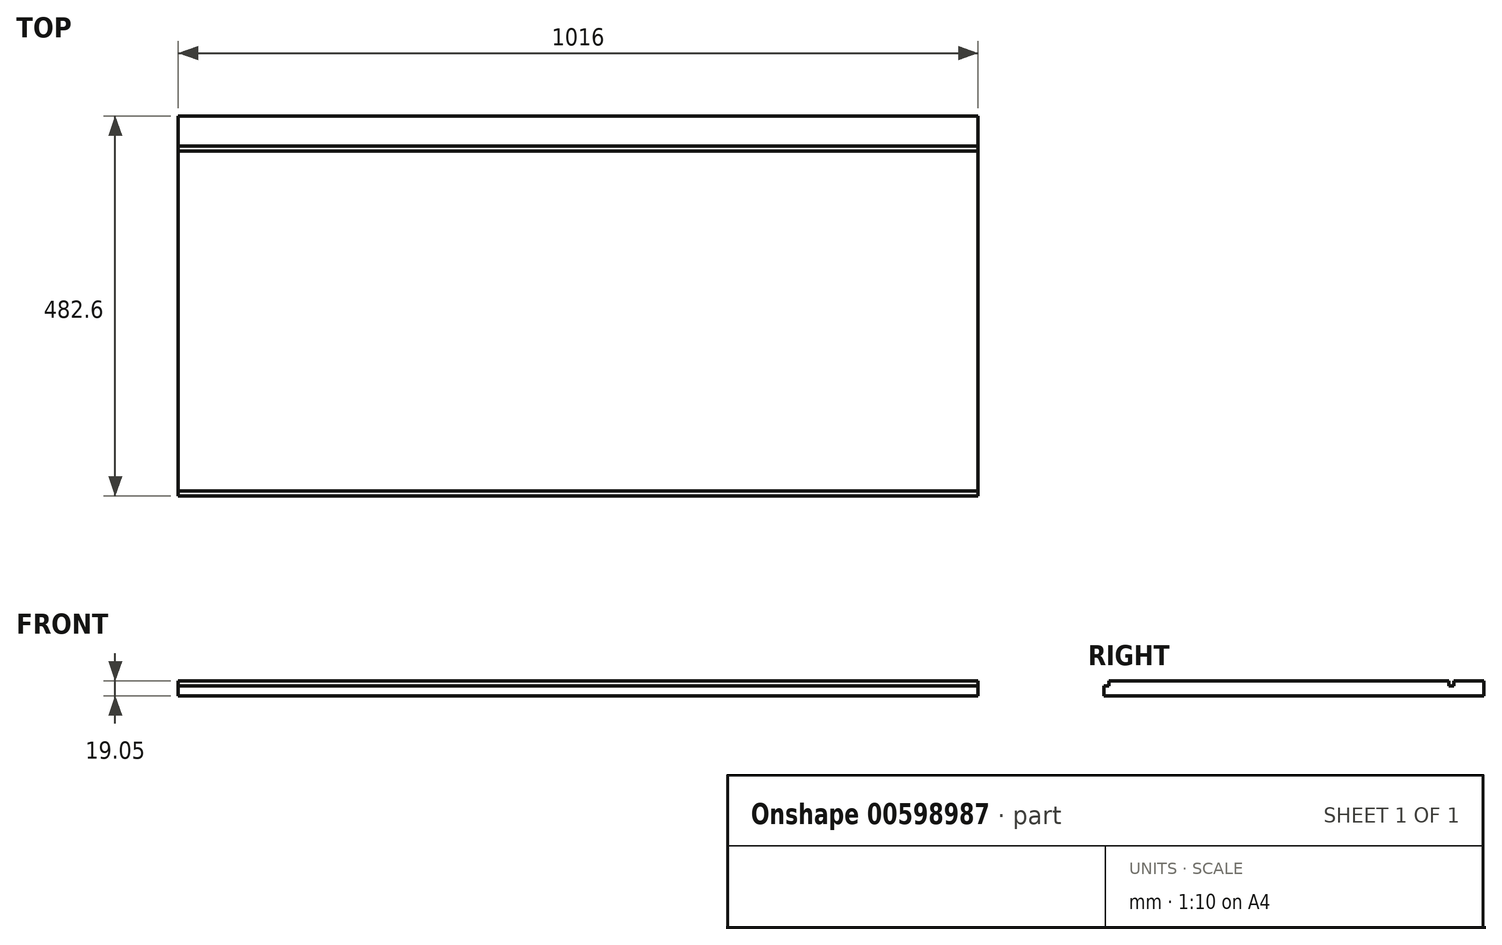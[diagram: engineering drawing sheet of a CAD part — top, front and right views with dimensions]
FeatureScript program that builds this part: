
annotation { "Feature Type Name" : "Feature", "Feature Type Description" : "" }
export const myFeature = defineFeature(function(context is Context, id is Id, definition is map)
    precondition{}
    {
        {
            var Q0;
            Q0=qCreatedBy(makeId("Top.planeOp"),FACE);
            var sketch = newSketch(context, id + "F0", { "sketchPlane" : qUnion([Q0])});
            skLineSegment(sketch, "E0.bottom", {"start": v(3.46, 11.02) * mm, "end": v(1019.46, 11.02) * mm});
            skLineSegment(sketch, "E0.top", {"start": v(3.46, 493.62) * mm, "end": v(1019.46, 493.62) * mm});
            skLineSegment(sketch, "E0.left", {"start": v(3.46, 11.02) * mm, "end": v(3.46, 493.62) * mm});
            skLineSegment(sketch, "E0.right", {"start": v(1019.46, 11.02) * mm, "end": v(1019.46, 493.62) * mm});
            skSolve(sketch);
        }
        {
            var Q0;
            Q0 = qSketchRegion(id + "F0", true);
            extrude(context, id + "F1", {"entities" : qUnion([Q0]), "depth" : 19.05 * mm, "offsetDistance" : 25.4 * mm});
        }
        {
            var Q0;
            Q0=makeQuery(id+"F1.opExtrude","CAP_FACE",FACE,{"disambiguationData":[OSD([sQuery(id+"F0.wireOp",EDGE,"E0.bottom"),sQuery(id+"F0.wireOp",EDGE,"E0.top"),sQuery(id+"F0.wireOp",EDGE,"E0.left"),sQuery(id+"F0.wireOp",EDGE,"E0.right")])],"isStart":false});
            var sketch = newSketch(context, id + "F2", { "sketchPlane" : qUnion([Q0])});
            skLineSegment(sketch, "E1.bottom", {"start": v(3.46, 455.52) * mm, "end": v(1019.46, 455.52) * mm});
            skLineSegment(sketch, "E1.top", {"start": v(3.46, 449.17) * mm, "end": v(1019.46, 449.17) * mm});
            skLineSegment(sketch, "E1.left", {"start": v(3.46, 455.52) * mm, "end": v(3.46, 449.17) * mm});
            skLineSegment(sketch, "E1.right", {"start": v(1019.46, 455.52) * mm, "end": v(1019.46, 449.17) * mm});
            skLineSegment(sketch, "E2.bottom", {"start": v(3.46, 11.02) * mm, "end": v(1019.46, 11.02) * mm});
            skLineSegment(sketch, "E2.top", {"start": v(3.46, 17.37) * mm, "end": v(1019.46, 17.37) * mm});
            skLineSegment(sketch, "E2.left", {"start": v(3.46, 11.02) * mm, "end": v(3.46, 17.37) * mm});
            skLineSegment(sketch, "E2.right", {"start": v(1019.46, 11.02) * mm, "end": v(1019.46, 17.37) * mm});
            skSolve(sketch);
        }
        {
            var Q0;
            Q0 = qSketchRegion(id + "F2", true);
            extrude(context, id + "F3", {"entities" : qUnion([Q0]), "operationType" : NewBodyOperationType.REMOVE, "oppositeDirection" : true, "depth" : 6.35 * mm, "offsetDistance" : 25.4 * mm});
        }
    });
